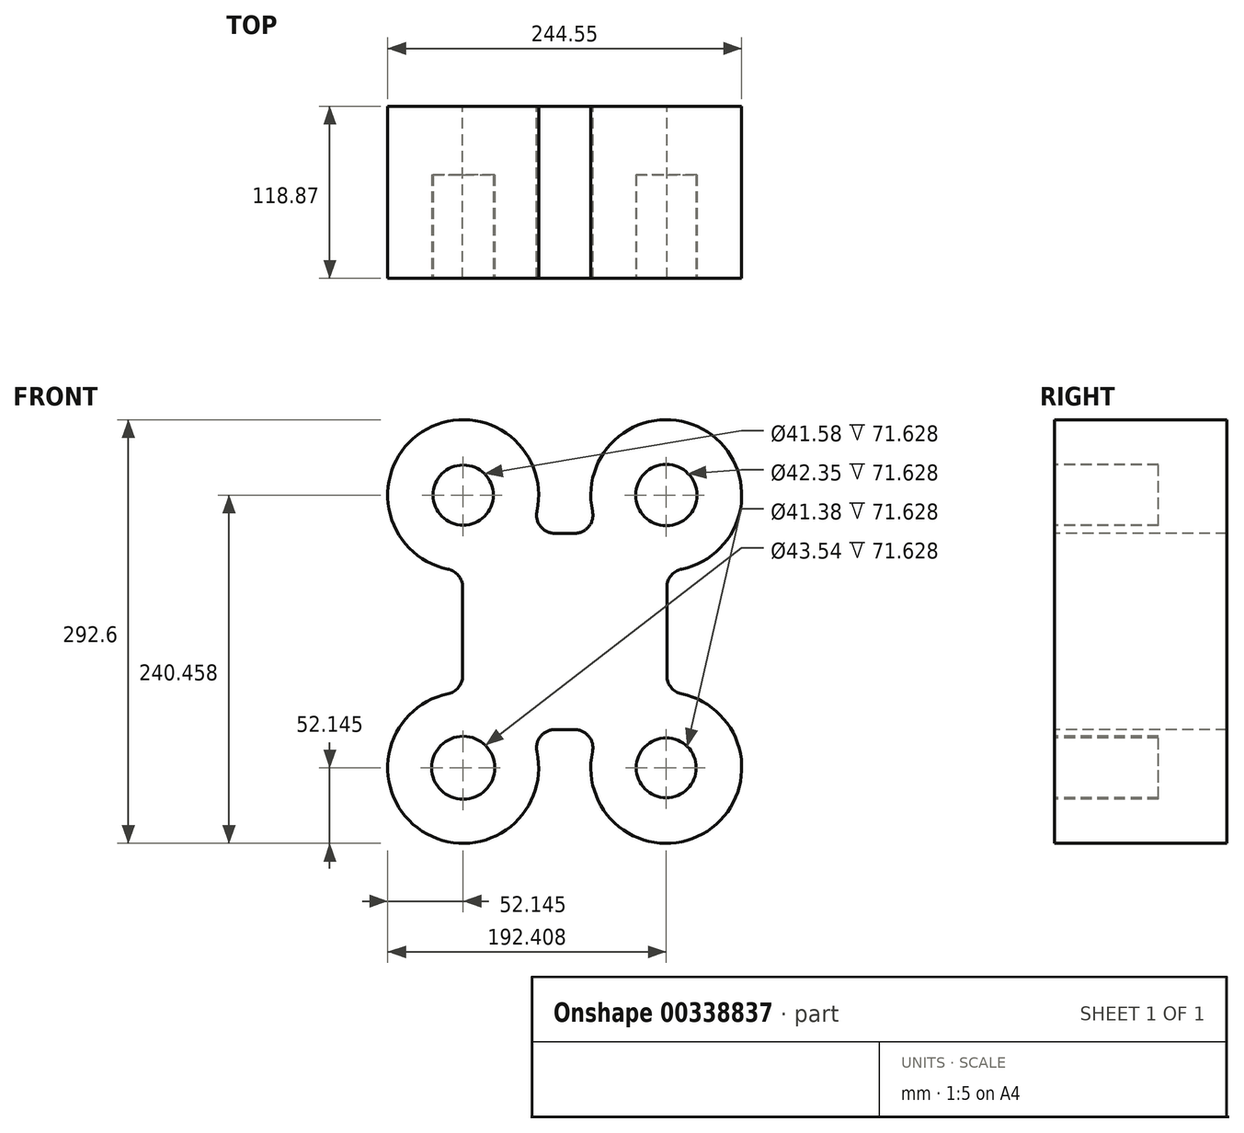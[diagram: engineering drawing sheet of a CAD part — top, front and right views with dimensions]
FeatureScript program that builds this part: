
annotation { "Feature Type Name" : "Feature", "Feature Type Description" : "" }
export const myFeature = defineFeature(function(context is Context, id is Id, definition is map)
    precondition{}
    {
        {
            var Q0;
            Q0=qCreatedBy(makeId("Front.planeOp"),FACE);
            var sketch = newSketch(context, id + "F0", { "sketchPlane" : qUnion([Q0])});
            skLineSegment(sketch, "E0.bottom", {"start": v(-119.22, 52.15) * mm, "end": v(-48.65, 52.15) * mm});
            skLineSegment(sketch, "E0.top", {"start": v(-119.22, -15.58) * mm, "end": v(-94.04, -15.58) * mm});
            skLineSegment(sketch, "E0.left", {"start": v(-119.22, 52.15) * mm, "end": v(-119.22, -15.58) * mm});
            skLineSegment(sketch, "E0.right", {"start": v(-48.65, 52.15) * mm, "end": v(-48.65, 10.14) * mm});
            skArc(sketch, "E1", {"start": v(-94.04, -15.58) * mm, "mid": v(-23.39, -87.37) * mm, "end": v(-48.65, 10.14) * mm});
            skSolve(sketch);
        }
        {
            var Q0;
            Q0 = qSketchRegion(id + "F0", true);
            extrude(context, id + "F1", {"entities" : qUnion([Q0]), "depth" : 118.87 * mm});
        }
        {
            var Q0;
            Q0=makeQuery(id+"F1.opExtrude","SWEPT_EDGE",EDGE,{"disambiguationData":[OSD([sQuery(id+"F0.wireOp",EDGE,"E0.top"),sQuery(id+"F0.wireOp",EDGE,"E1")])]});
            var Q1;
            Q1=makeQuery(id+"F1.opExtrude","SWEPT_EDGE",EDGE,{"disambiguationData":[OSD([sQuery(id+"F0.wireOp",EDGE,"E0.right"),sQuery(id+"F0.wireOp",EDGE,"E1")])]});
            fillet(context, id + "F2", {"entities" : qUnion([Q0, Q1]), "radius" : 12.7 * mm, "tangentPropagation" : true, "allowEdgeOverflow" : false});
        }
        {
            var Q0;
            Q0=makeQuery(id+"F1.opExtrude","SWEPT_BODY",BODY,{"disambiguationData":[OSD([sQuery(id+"F0.wireOp",EDGE,"E0.bottom"),sQuery(id+"F0.wireOp",EDGE,"E0.top"),sQuery(id+"F0.wireOp",EDGE,"E0.left"),sQuery(id+"F0.wireOp",EDGE,"E0.right"),sQuery(id+"F0.wireOp",EDGE,"E1")])]});
            var Q1;
            Q1=makeQuery(id+"F1.opExtrude","SWEPT_FACE",FACE,{"disambiguationData":[OSD([sQuery(id+"F0.wireOp",EDGE,"E0.left")])]});
            mirror(context, id + "F3", {"operationType" : NewBodyOperationType.ADD, "entities" : qUnion([Q0]), "mirrorPlane" : qUnion([Q1])});
        }
        {
            var Q0;
            Q0=makeQuery(id+"F1.opExtrude","SWEPT_BODY",BODY,{"disambiguationData":[OSD([sQuery(id+"F0.wireOp",EDGE,"E0.bottom"),sQuery(id+"F0.wireOp",EDGE,"E0.top"),sQuery(id+"F0.wireOp",EDGE,"E0.left"),sQuery(id+"F0.wireOp",EDGE,"E0.right"),sQuery(id+"F0.wireOp",EDGE,"E1")])]});
            var Q1;
            {var subQ0=makeQuery(id+"F1.opExtrude","SWEPT_FACE",FACE,{"disambiguationData":[OSD([sQuery(id+"F0.wireOp",EDGE,"E0.bottom")])]});Q1=makeQuery(id+"F3.boolean.opBoolean","MERGE",FACE,{"derivedFrom":[subQ0,makeQuery(id+"F3.opPattern","COPY",FACE,{"derivedFrom":subQ0,"instanceName":"1"})]});}
            mirror(context, id + "F4", {"operationType" : NewBodyOperationType.ADD, "entities" : qUnion([Q0]), "mirrorPlane" : qUnion([Q1])});
        }
        {
            var Q0;
            {var subQ0=makeQuery(id+"F1.opExtrude","CAP_FACE",FACE,{"disambiguationData":[OSD([sQuery(id+"F0.wireOp",EDGE,"E0.bottom"),sQuery(id+"F0.wireOp",EDGE,"E0.top"),sQuery(id+"F0.wireOp",EDGE,"E0.left"),sQuery(id+"F0.wireOp",EDGE,"E0.right"),sQuery(id+"F0.wireOp",EDGE,"E1")])],"isStart":false});var subQ1=makeQuery(id+"F3.boolean.opBoolean","MERGE",FACE,{"derivedFrom":[subQ0,makeQuery(id+"F3.opPattern","COPY",FACE,{"derivedFrom":subQ0,"instanceName":"1"})]});Q0=makeQuery(id+"F4.boolean.opBoolean","MERGE",FACE,{"derivedFrom":[subQ1,makeQuery(id+"F4.opPattern","COPY",FACE,{"derivedFrom":subQ1,"instanceName":"1"})]});}
            var sketch = newSketch(context, id + "F5", { "sketchPlane" : qUnion([Q0])});
            skCircle(sketch, "E2", {"center": v(-189.35, 146.3) * mm, "radius": 20.79 * mm});
            skCircle(sketch, "E3", {"center": v(-49.1, 146.3) * mm, "radius": 21.18 * mm});
            skCircle(sketch, "E4", {"center": v(-49.1, -42) * mm, "radius": 20.69 * mm});
            skCircle(sketch, "E5", {"center": v(-189.35, -42) * mm, "radius": 21.77 * mm});
            skSolve(sketch);
        }
        {
            var Q0;
            Q0 = qSketchRegion(id + "F5", true);
            extrude(context, id + "F6", {"entities" : qUnion([Q0]), "operationType" : NewBodyOperationType.REMOVE, "oppositeDirection" : true, "depth" : 71.63 * mm});
        }
    });
